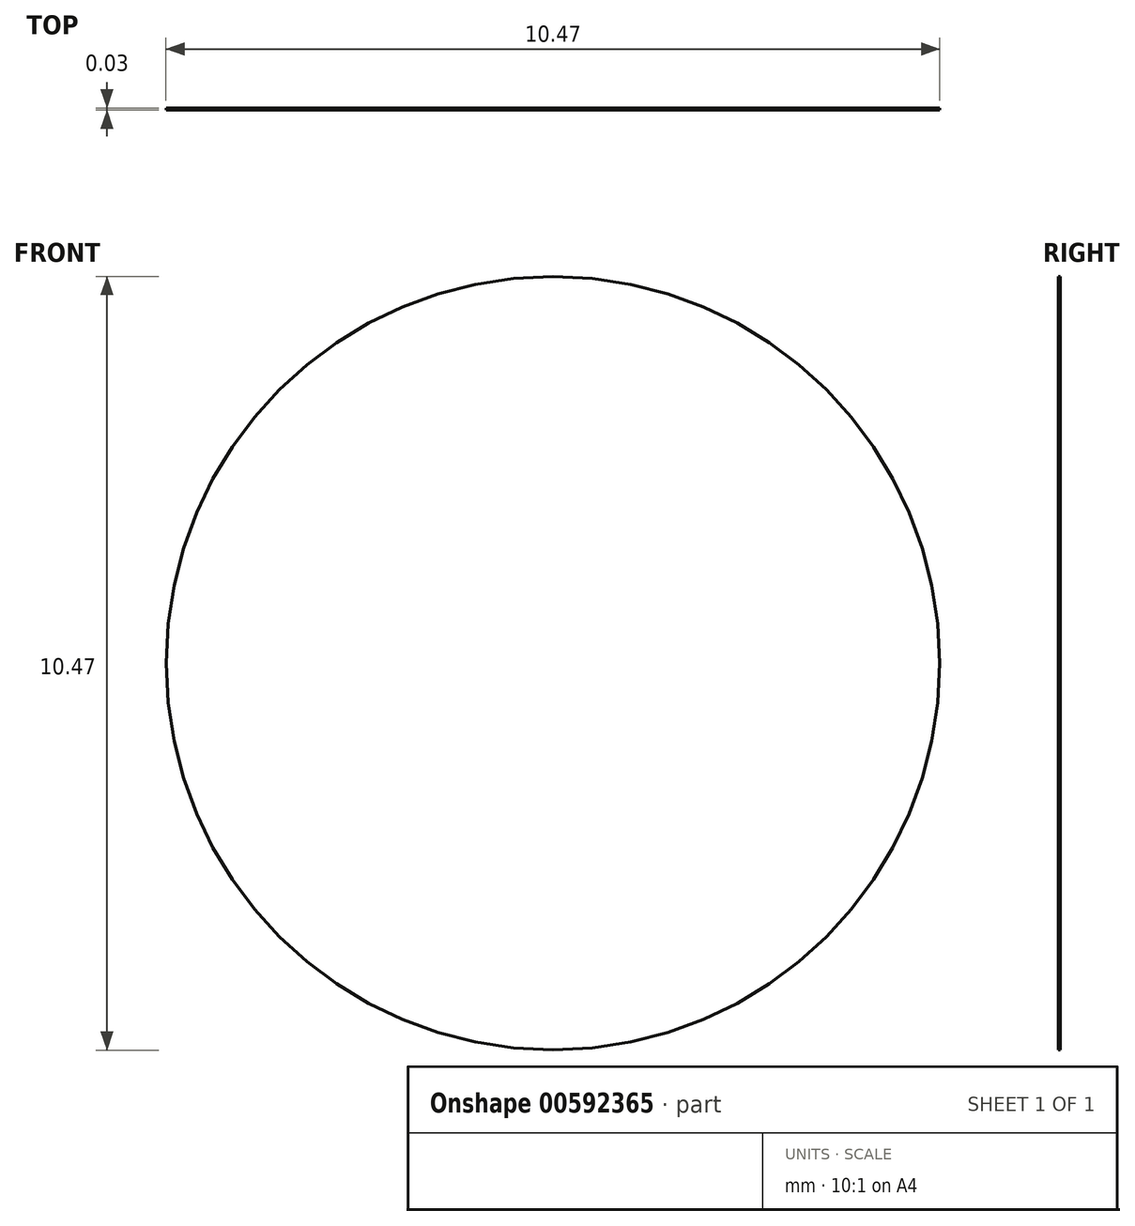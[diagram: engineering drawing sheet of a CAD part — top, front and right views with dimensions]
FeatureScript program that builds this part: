
annotation { "Feature Type Name" : "Feature", "Feature Type Description" : "" }
export const myFeature = defineFeature(function(context is Context, id is Id, definition is map)
    precondition{}
    {
        {
            var Q0;
            Q0=qCreatedBy(makeId("Front.planeOp"),FACE);
            var sketch = newSketch(context, id + "F0", { "sketchPlane" : qUnion([Q0])});
            skCircle(sketch, "E0", {"center": v(-12.38, 28.92) * mm, "radius": 5.23 * mm});
            skSolve(sketch);
        }
        {
            var Q0;
            Q0=makeQuery(id+"F0.imprint","IMPRINT",FACE,{"disambiguationData":[TD([[makeQuery(id+"F0.imprint","IMPRINT",EDGE,{"derivedFrom":sQuery(id+"F0.wireOp",EDGE,"E0")}),1.0]])]});
            extrude(context, id + "F1", {"entities" : qUnion([Q0]), "depth" : 0.03 * mm, "offsetDistance" : 25.4 * mm});
        }
    });
